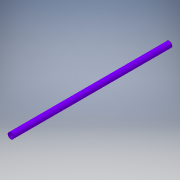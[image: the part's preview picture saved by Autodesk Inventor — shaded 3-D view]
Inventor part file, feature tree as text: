
AUTODESK INVENTOR PART (.ipt)
format: ipt  version: 2018.2 (Build 222227000, 227)  size: 105,984 bytes
history: native  units: in
note: dims shown in document units (in); Inventor stores cm internally (conversion verified against a paired STEP export)
features: extrude x1, sketch x1
ambient origin geometry x8: Origin, YZ Plane, XZ Plane, XY Plane, X Axis, Y Axis, Z Axis, Center Point
bodies: Solid1 (feature_tree)
feature tree (2):
  extrude  "Extrusion1"  Depth=36.0in
  sketch  "Sketch1"  dims[d0=1.315in d1=1.0in d2=36.0in d3=0.0in]
